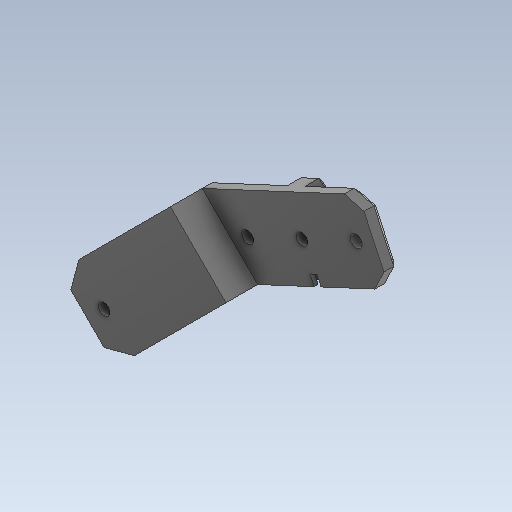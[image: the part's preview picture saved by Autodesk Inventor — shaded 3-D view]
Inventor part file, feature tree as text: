
AUTODESK INVENTOR PART (.ipt)
format: ipt  version: 2020 (Build 240168000, 168)  size: 250,880 bytes
history: native  units: in
note: dims shown in document units (in); Inventor stores cm internally (conversion verified against a paired STEP export)
features: sketch x15, other x3
ambient origin geometry x8: Origin, YZ Plane, XZ Plane, XY Plane, X Axis, Y Axis, Z Axis, Center Point
bodies: Solid1 (feature_tree)
feature tree (18):
  other  "TibiaTop.ipt"
  other  "Solid2::TibiaTop.ipt"
  other  "TaggingFeature1"
  sketch  "Sketch1"  dims[d0=0.3937in]
  sketch  "Sketch9"
  sketch  "Sketch10"
  sketch  "Sketch11"
  sketch  "Sketch15"
  sketch  "Sketch25"
  sketch  "Sketch26"
  sketch  "Sketch27"
  sketch  "Sketch29"
  sketch  "Sketch30"
  sketch  "Sketch31"
  sketch  "Sketch32"
  sketch  "Sketch34"
  sketch  "Sketch35"
  sketch  "Sketch37"
